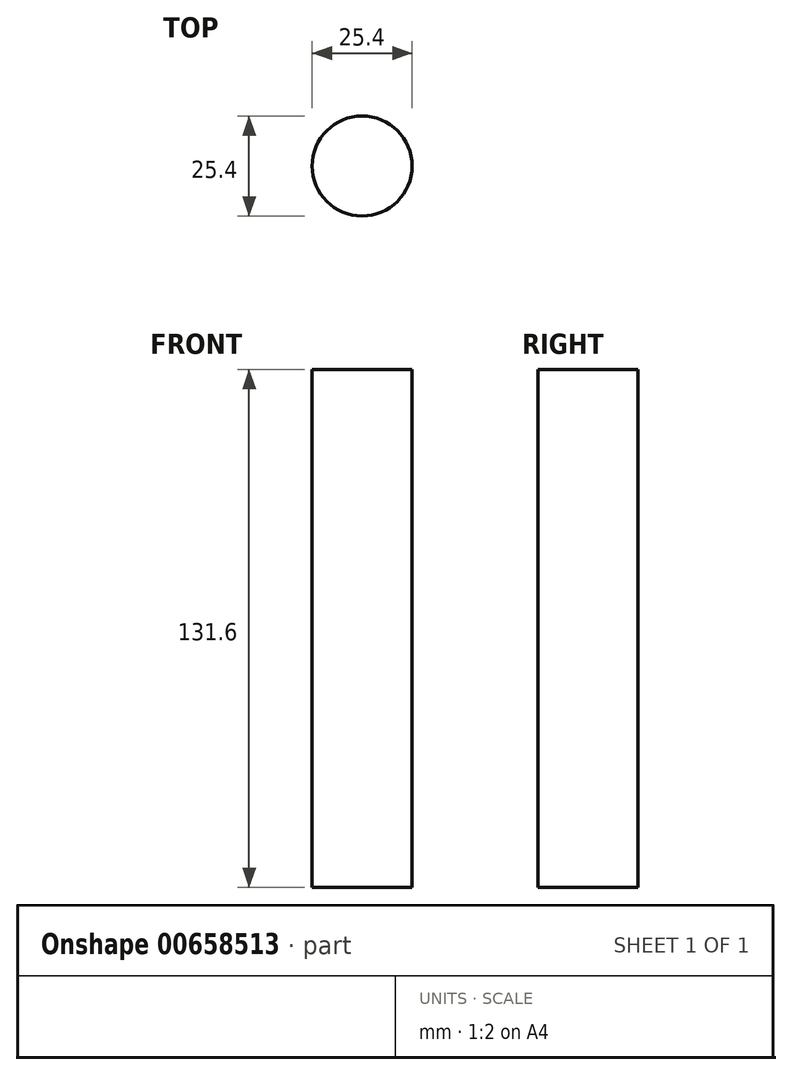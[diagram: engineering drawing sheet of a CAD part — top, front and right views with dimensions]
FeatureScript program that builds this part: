
annotation { "Feature Type Name" : "Feature", "Feature Type Description" : "" }
export const myFeature = defineFeature(function(context is Context, id is Id, definition is map)
    precondition{}
    {
        {
            var Q0;
            Q0=qCreatedBy(makeId("Top.planeOp"),FACE);
            var sketch = newSketch(context, id + "F0", { "sketchPlane" : qUnion([Q0])});
            skCircle(sketch, "E0", {"center": v(0, 0) * mm, "radius": 12.7 * mm});
            skSolve(sketch);
        }
        {
            var Q0;
            Q0=makeQuery(id+"F0.imprint","IMPRINT",FACE,{"disambiguationData":[TD([[makeQuery(id+"F0.imprint","IMPRINT",EDGE,{"derivedFrom":sQuery(id+"F0.wireOp",EDGE,"E0")}),1.0]])]});
            extrude(context, id + "F1", {"entities" : qUnion([Q0]), "oppositeDirection" : true, "depth" : 131.6 * mm, "offsetDistance" : 25.4 * mm});
        }
    });
